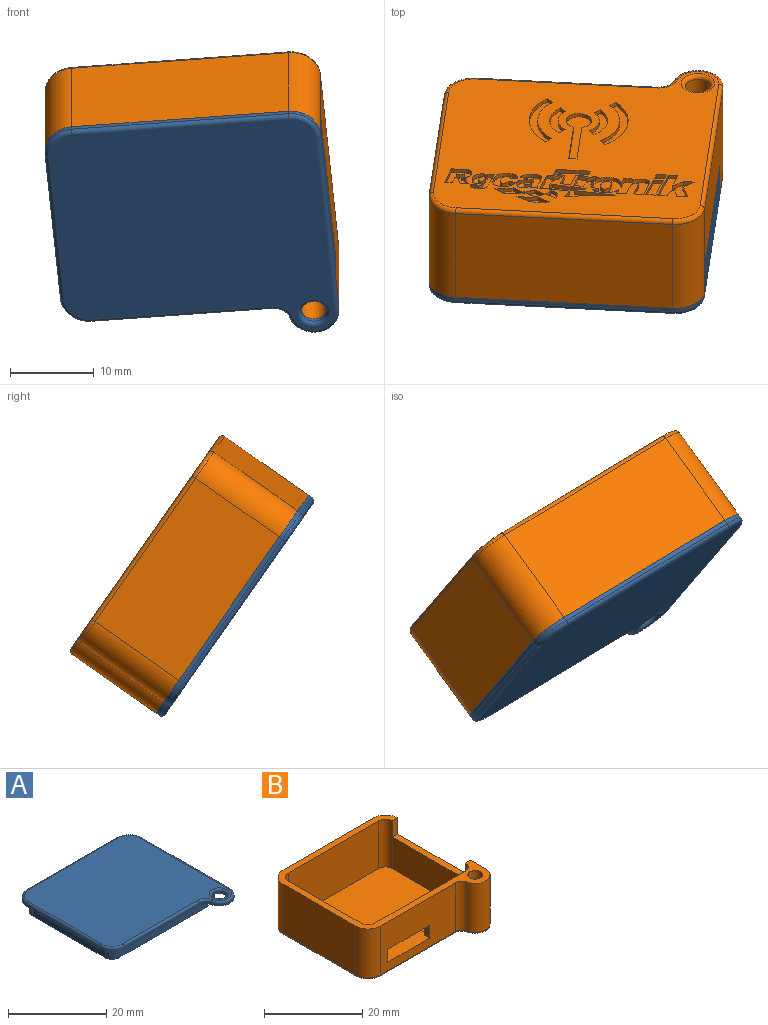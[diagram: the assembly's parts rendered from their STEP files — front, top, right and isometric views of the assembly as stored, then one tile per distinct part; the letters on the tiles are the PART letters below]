
ASSEMBLY  parts=2 mates=1
PART A: 39 faces, bbox 33.6x32.5x5 mm
  f0: plane 33x31.91mm, normal (0,0,-1), area 820.6mm2, adj f1,f2,f3,f4,f5,f6,f7,f8
  f1: plane 25.48x3mm, normal (0,1,0), area 76.4mm2, adj f0,f2,f9,f13
  f2: cylinder r=2mm len=3mm, axis (0,0,1), area 9.4mm2, adj f0,f1,f3,f13
  f3: plane 20.96x3mm, normal (-1,0,0), area 62.9mm2, adj f0,f2,f4,f13
  f4: cylinder r=2mm len=3mm, axis (0,0,1), area 9.4mm2, adj f0,f3,f5,f13
  f5: plane 25.48x3mm, normal (0,-1,0), area 76.4mm2, adj f0,f4,f6,f13
  f6: cylinder r=0.5mm len=3mm, axis (0,0,1), area 4.7mm2, adj f0,f5,f7,f13
  f7: plane 25.48x3mm, normal (0,1,0), area 76.4mm2, adj f0,f6,f10,f13
  f8: plane 25.48x3mm, normal (0,-1,0), area 76.4mm2, adj f0,f9,f12,f13
  f9: cylinder r=0.5mm len=3mm, axis (0,0,1), area 4.7mm2, adj f0,f1,f8,f13
  f10: cylinder r=1mm len=3mm, axis (0,0,1), area 4.7mm2, adj f0,f7,f11,f13
  f11: plane 20.96x3mm, normal (1,0,0), area 62.9mm2, adj f0,f10,f12,f13
  f12: cylinder r=1mm len=3mm, axis (0,0,1), area 4.7mm2, adj f0,f8,f11,f13
  f13: plane 27.98x24.96mm, normal (0,0,-1), area 77.4mm2, adj f1,f2,f3,f4,f5,f6,f7,f8
  f14: plane 26x0.5mm, normal (0,1,0), area 13mm2, adj f0,f15,f23,f37
  f15: cylinder r=3.5mm len=3.5mm, axis (0,0,1), area 2.7mm2, adj f0,f14,f16,f35
  f16: plane 21x0.5mm, normal (-1,0,0), area 10.5mm2, adj f0,f15,f17,f33
  f17: cylinder r=3.5mm len=3.5mm, axis (0,0,1), area 2.7mm2, adj f0,f16,f18,f31
  f18: plane 21.62x0.5mm, normal (0,-1,0), area 10.8mm2, adj f0,f17,f19,f30
  f19: cylinder r=2mm len=1.95mm, axis (0,0,1), area 1.4mm2, adj f0,f18,f20,f32
  f20: cylinder r=3mm len=5.93mm, axis (0,0,1), area 4.4mm2, adj f0,f19,f21,f34
  f21: plane 25.41x4.5mm, normal (1,0,0), area 96.3mm2, adj f0,f20,f23,f25,f26,f27,f36
  f22: cylinder r=1.5mm len=3mm, axis (0,0,1), area 4.7mm2, adj f0,f29
  f23: cylinder r=3.5mm len=3.5mm, axis (0,0,1), area 2.7mm2, adj f0,f14,f21,f38
  f24: plane 32x30.91mm, normal (0,0,1), area 863.6mm2, adj f29,f30,f31,f32,f33,f34,f35,f36
  f25: plane 4x1.5mm, normal (0,-1,0), area 6mm2, adj f0,f21,f26,f28
  f26: plane 20.9x1.5mm, normal (0,0,-1), area 31.3mm2, adj f21,f25,f27,f28
  f27: plane 4x1.5mm, normal (0,1,0), area 6mm2, adj f0,f21,f26,f28
  f28: plane 20.9x4mm, normal (-1,0,0), area 83.6mm2, adj f0,f25,f26,f27
  f29: torus R=2mm, axis (0,0,1), area 8.3mm2, adj f22,f24
  f30: cylinder r=0.5mm len=21.62mm, axis (1,0,0), area 17mm2, adj f18,f24,f31,f32
  f31: torus R=3mm, axis (0,0,1), area 4.1mm2, adj f17,f24,f30,f33
  f32: torus R=2.5mm, axis (0,0,1), area 2.3mm2, adj f19,f24,f30,f34
  f33: cylinder r=0.5mm len=21mm, axis (0,-1,0), area 16.5mm2, adj f16,f24,f31,f35
  f34: torus R=2.5mm, axis (0,0,1), area 6.5mm2, adj f20,f24,f32,f36
  f35: torus R=3mm, axis (0,0,1), area 4.1mm2, adj f15,f24,f33,f37
  f36: cylinder r=0.5mm len=25.41mm, axis (0,1,0), area 20mm2, adj f21,f24,f34,f38
  f37: cylinder r=0.5mm len=26mm, axis (-1,0,0), area 20.4mm2, adj f14,f24,f35,f38
  f38: torus R=3mm, axis (0,0,1), area 4.1mm2, adj f23,f24,f36,f37
PART B: 193 faces, bbox 33.6x32.5x12.7 mm
  f0: plane 30x25mm, normal (0,0,1), area 671.6mm2, adj f2,f4,f5,f6,f7,f8,f9,f10
  f1: plane 32x30.91mm, normal (0,0,-1), area 738.5mm2, adj f21,f22,f23,f24,f25,f26,f27,f28
  f2: plane 21x7.9mm, normal (-1,0,0), area 165.9mm2, adj f0,f7,f8,f31
  f3: plane 33x31.91mm, normal (0,0,1), area 151.3mm2, adj f4,f5,f6,f7,f8,f9,f10,f11
  f4: plane 26x11.9mm, normal (0,-1,0), area 309.4mm2, adj f0,f3,f7,f10
  f5: plane 21x11.9mm, normal (1,0,0), area 249.9mm2, adj f0,f3,f9,f10
  f6: plane 26x11.9mm, normal (0,1,0), area 244mm2, adj f0,f3,f8,f9,f34,f35,f36,f37
  f7: cylinder r=2mm len=11.9mm, axis (0,0,-1), area 37.4mm2, adj f0,f2,f3,f4,f33
  f8: cylinder r=2mm len=11.9mm, axis (0,0,-1), area 37.4mm2, adj f0,f2,f3,f6,f32
  f9: cylinder r=2mm len=11.9mm, axis (0,0,-1), area 37.4mm2, adj f0,f3,f5,f6,f192
  f10: cylinder r=2mm len=11.9mm, axis (0,0,-1), area 37.4mm2, adj f0,f3,f4,f5
  f11: plane 26x12.2mm, normal (0,1,0), area 317.2mm2, adj f3,f12,f19,f28
  f12: cylinder r=3.5mm len=12.2mm, axis (0,0,-1), area 67.1mm2, adj f3,f11,f13,f26
  f13: plane 21x12.2mm, normal (-1,0,0), area 256.2mm2, adj f3,f12,f14,f24
  f14: cylinder r=3.5mm len=12.2mm, axis (0,0,-1), area 67.1mm2, adj f3,f13,f15,f22
  f15: plane 21.62x12.2mm, normal (0,-1,0), area 225.4mm2, adj f3,f14,f16,f21,f34,f35,f36,f37
  f16: cylinder r=2mm len=12.2mm, axis (0,0,-1), area 33mm2, adj f3,f15,f17,f23
  f17: cylinder r=3mm len=12.2mm, axis (0,0,-1), area 107mm2, adj f3,f16,f18,f25
  f18: plane 25.41x12.2mm, normal (1,0,0), area 226.1mm2, adj f3,f17,f19,f27,f31,f32
  f19: cylinder r=3.5mm len=12.2mm, axis (0,0,-1), area 67.1mm2, adj f3,f11,f18,f29,f33
  f20: cylinder r=1.5mm len=12.2mm, axis (0,0,-1), area 115mm2, adj f3,f30
  f21: cylinder r=0.5mm len=21.62mm, axis (1,0,0), area 17mm2, adj f1,f15,f22,f23
  f22: torus R=3mm, axis (0,0,1), area 4.1mm2, adj f1,f14,f21,f24
  f23: torus R=2.5mm, axis (0,0,1), area 2.3mm2, adj f1,f16,f21,f25
  f24: cylinder r=0.5mm len=21mm, axis (0,-1,0), area 16.5mm2, adj f1,f13,f22,f26
  f25: torus R=2.5mm, axis (0,0,1), area 6.5mm2, adj f1,f17,f23,f27
  f26: torus R=3mm, axis (0,0,1), area 4.1mm2, adj f1,f12,f24,f28
  f27: cylinder r=0.5mm len=25.41mm, axis (0,1,0), area 20mm2, adj f1,f18,f25,f29
  f28: cylinder r=0.5mm len=26mm, axis (-1,0,0), area 20.4mm2, adj f1,f11,f26,f29
  f29: torus R=3mm, axis (0,0,1), area 4.1mm2, adj f1,f19,f27,f28
  f30: torus R=2mm, axis (0,0,1), area 8.3mm2, adj f1,f20
  f31: plane 21x1.5mm, normal (0,0,1), area 31.5mm2, adj f2,f18,f32,f33
  f32: plane 4x1.5mm, normal (0,1,0), area 6mm2, adj f3,f8,f18,f31
  f33: plane 4x1.5mm, normal (0,-1,0), area 6mm2, adj f3,f7,f19,f31
  f34: plane 3.2x1.5mm, normal (1,0,0), area 4.8mm2, adj f6,f15,f35,f37
  f35: plane 15x6.5mm, normal (0,0,1), area 93mm2, adj f6,f15,f34,f36,f190,f191,f192
  f36: plane 3.2x1.5mm, normal (-1,0,0), area 4.8mm2, adj f6,f15,f35,f37
  f37: plane 12x1.5mm, normal (0,0,-1), area 18mm2, adj f6,f15,f34,f36
  f38: plane 2.92x0.56mm, normal (0.98,0.19,0), area 1.5mm2, adj f1,f39,f48,f49
  f39: plane 0.93x0.5mm, normal (0.02,-1,0), area 0.5mm2, adj f1,f38,f40,f49
  f40: extruded ~1.23x0.96mm, area 1.4mm2, adj f1,f39,f41,f49
  f41: plane 0.95x0.5mm, normal (0,-1,0), area 0.5mm2, adj f1,f40,f42,f49
  f42: extruded ~1.25x0.65mm, area 0.7mm2, adj f1,f41,f43,f49
  f43: extruded ~1.67x1.11mm, area 1.7mm2, adj f1,f42,f48,f49
  f44: extruded ~0.58x0.53mm, area 0.6mm2, adj f45,f47,f49,f50
  f45: plane 0.5x0.44mm, normal (0,1,0), area 0.2mm2, adj f44,f46,f49,f50
  f46: plane 0.58x0.5mm, normal (-0.98,-0.19,0), area 0.3mm2, adj f45,f47,f49,f50
  f47: plane 0.5x0.5mm, normal (0,-1,0), area 0.2mm2, adj f44,f46,f49,f50
  f48: plane 1.83x0.5mm, normal (0,1,0), area 0.9mm2, adj f1,f38,f43,f49
  f49: plane 3.22x2.95mm, normal (0,0,-1), area 6.1mm2, adj f38,f39,f40,f41,f42,f43,f44,f45
  f50: plane 0.97x0.58mm, normal (0,0,-1), area 0.5mm2, adj f44,f45,f46,f47
  f51: cylinder r=2.45mm len=3.72mm, axis (0,0,-1), area 2.1mm2, adj f1,f52,f54,f55
  f52: plane 0.8x0.6mm, normal (0.8,-0.6,0), area 0.5mm2, adj f1,f51,f53,f55
  f53: cylinder r=3.45mm len=5.24mm, axis (0,0,-1), area 3mm2, adj f1,f52,f54,f55
  f54: plane 0.71x0.7mm, normal (0.71,0.7,0), area 0.5mm2, adj f1,f51,f53,f55
  f55: plane 5.24x1.99mm, normal (0,0,-1), area 5.1mm2, adj f51,f52,f53,f54
  f56: plane 6.59x0.5mm, normal (-1,0,0), area 3.3mm2, adj f1,f57,f59,f60
  f57: cylinder r=1.5mm len=3mm, axis (0,0,-1), area 4.2mm2, adj f1,f56,f58,f60
  f58: plane 6.59x0.5mm, normal (1,0,0), area 3.3mm2, adj f1,f57,f59,f60
  f59: plane 1x0.5mm, normal (0,-1,0), area 0.5mm2, adj f1,f56,f58,f60
  f60: plane 9.5x3mm, normal (0,0,-1), area 13.6mm2, adj f56,f57,f58,f59
  f61: plane 0.71x0.7mm, normal (0.71,0.7,0), area 0.5mm2, adj f1,f62,f64,f65
  f62: cylinder r=4.91mm len=7.44mm, axis (0,0,-1), area 4.2mm2, adj f1,f61,f63,f65
  f63: plane 0.8x0.6mm, normal (0.8,-0.6,0), area 0.5mm2, adj f1,f62,f64,f65
  f64: cylinder r=5.91mm len=8.96mm, axis (0,0,-1), area 5.1mm2, adj f1,f61,f63,f65
  f65: plane 8.96x2.97mm, normal (0,0,-1), area 9.3mm2, adj f61,f62,f63,f64
  f66: extruded ~2.89x2.89mm, area 4.2mm2, adj f1,f67,f69,f70
  f67: plane 0.84x0.5mm, normal (-0.14,0.99,0), area 0.4mm2, adj f1,f66,f68,f70
  f68: extruded ~1.46x1.18mm, area 1.8mm2, adj f1,f67,f69,f70
  f69: plane 0.84x0.5mm, normal (-0.06,-1,0), area 0.4mm2, adj f1,f66,f68,f70
  f70: plane 2.9x2.9mm, normal (0,0,-1), area 4.8mm2, adj f66,f67,f68,f69
  f71: plane 1.44x0.5mm, normal (0,-1,0), area 0.7mm2, adj f1,f72,f78,f79
  f72: plane 1.07x0.5mm, normal (-0.98,-0.19,0), area 0.5mm2, adj f1,f71,f73,f79
  f73: plane 4.07x0.5mm, normal (0,1,0), area 2mm2, adj f1,f72,f74,f79
  f74: plane 1.08x0.5mm, normal (0.98,0.19,0), area 0.6mm2, adj f1,f73,f75,f79
  f75: plane 1.32x0.5mm, normal (0,-1,0), area 0.7mm2, adj f1,f74,f76,f79
  f76: plane 1.81x0.5mm, normal (0.98,0.21,0), area 0.9mm2, adj f1,f75,f77,f79
  f77: plane 1.24x0.5mm, normal (0.12,-0.99,0), area 0.6mm2, adj f1,f76,f78,f79
  f78: plane 1.99x0.5mm, normal (-0.97,-0.22,0), area 1mm2, adj f1,f71,f77,f79
  f79: plane 4.27x3.05mm, normal (0,0,-1), area 6.8mm2, adj f71,f72,f73,f74,f75,f76,f77,f78
  f80: plane 3.11x0.65mm, normal (-0.98,-0.21,0), area 1.6mm2, adj f1,f81,f83,f84
  f81: plane 1.19x0.5mm, normal (0,1,0), area 0.6mm2, adj f1,f80,f82,f84
  f82: plane 3.11x0.65mm, normal (0.98,0.21,0), area 1.6mm2, adj f1,f81,f83,f84
  f83: plane 1.19x0.5mm, normal (0,-1,0), area 0.6mm2, adj f1,f80,f82,f84
  f84: plane 3.11x1.84mm, normal (0,0,-1), area 3.7mm2, adj f80,f81,f82,f83
  f85: extruded ~2.19x0.5mm, area 1.1mm2, adj f1,f86,f88,f89
  f86: plane 1.18x0.8mm, normal (0.56,-0.83,0), area 0.7mm2, adj f1,f85,f87,f89
  f87: extruded ~2.46x0.5mm, area 1.2mm2, adj f1,f86,f88,f89
  f88: plane 1.45x0.95mm, normal (-0.55,0.84,0), area 0.9mm2, adj f1,f85,f87,f89
  f89: plane 3.64x1.16mm, normal (0,0,-1), area 2.4mm2, adj f85,f86,f87,f88
  f90: extruded ~2.45x0.5mm, area 1.2mm2, adj f1,f91,f93,f94
  f91: plane 1.73x0.92mm, normal (0.47,-0.88,0), area 1mm2, adj f1,f90,f92,f94
  f92: extruded ~2.2x0.5mm, area 1.1mm2, adj f1,f91,f93,f94
  f93: plane 1.49x0.97mm, normal (-0.55,0.84,0), area 0.9mm2, adj f1,f90,f92,f94
  f94: plane 3.93x1.14mm, normal (0,0,-1), area 2.5mm2, adj f90,f91,f92,f93
  f95: plane 1.27x0.84mm, normal (-0.55,0.83,0), area 0.8mm2, adj f1,f96,f98,f99
  f96: extruded ~1.29x0.56mm, area 0.7mm2, adj f1,f95,f97,f99
  f97: plane 1.28x0.83mm, normal (0.55,-0.84,0), area 0.8mm2, adj f1,f96,f98,f99
  f98: extruded ~1.28x0.55mm, area 0.7mm2, adj f1,f95,f97,f99
  f99: plane 2.55x1.39mm, normal (0,0,-1), area 1.8mm2, adj f95,f96,f97,f98
  f100: plane 0.83x0.64mm, normal (-0.61,0.79,0), area 0.5mm2, adj f1,f101,f103,f104
  f101: extruded ~0.87x0.62mm, area 0.5mm2, adj f1,f100,f102,f104
  f102: plane 1.28x0.85mm, normal (0.55,-0.83,0), area 0.8mm2, adj f1,f101,f103,f104
  f103: extruded ~1.08x0.5mm, area 0.6mm2, adj f1,f100,f102,f104
  f104: plane 1.72x1.47mm, normal (0,0,-1), area 1.3mm2, adj f100,f101,f102,f103
  f105: plane 0.8x0.6mm, normal (-0.8,-0.6,0), area 0.5mm2, adj f1,f106,f108,f109
  f106: cylinder r=4.91mm len=7.44mm, axis (0,0,-1), area 4.2mm2, adj f1,f105,f107,f109
  f107: plane 0.71x0.7mm, normal (-0.71,0.7,0), area 0.5mm2, adj f1,f106,f108,f109
  f108: cylinder r=5.91mm len=8.96mm, axis (0,0,-1), area 5.1mm2, adj f1,f105,f107,f109
  f109: plane 8.96x2.97mm, normal (0,0,-1), area 9.3mm2, adj f105,f106,f107,f108
  f110: plane 0.8x0.6mm, normal (-0.8,-0.6,0), area 0.5mm2, adj f1,f111,f113,f114
  f111: cylinder r=2.45mm len=3.72mm, axis (0,0,-1), area 2.1mm2, adj f1,f110,f112,f114
  f112: plane 0.71x0.7mm, normal (-0.71,0.7,0), area 0.5mm2, adj f1,f111,f113,f114
  f113: cylinder r=3.45mm len=5.24mm, axis (0,0,-1), area 3mm2, adj f1,f110,f112,f114
  f114: plane 5.24x1.99mm, normal (0,0,-1), area 5.1mm2, adj f110,f111,f112,f113
  f115: plane 1.98x0.5mm, normal (-0.98,-0.21,0), area 1mm2, adj f1,f116,f136,f138
  f116: extruded ~2.08x1.17mm, area 1.6mm2, adj f1,f115,f117,f138
  f117: plane 0.5x0.49mm, normal (-0.98,-0.18,0), area 0.2mm2, adj f1,f116,f118,f138
  f118: plane 1.13x0.5mm, normal (0,1,0), area 0.6mm2, adj f1,f117,f119,f138
  f119: plane 1.13x0.5mm, normal (0.98,0.18,0), area 0.6mm2, adj f1,f118,f120,f138
  f120: extruded ~3.1x1.2mm, area 1.9mm2, adj f1,f119,f121,f138
  f121: plane 0.5x0.48mm, normal (-0.9,-0.45,0), area 0.3mm2, adj f1,f120,f122,f138
  f122: extruded ~1.37x0.71mm, area 0.8mm2, adj f1,f121,f123,f138
  f123: plane 0.61x0.5mm, normal (-0.98,-0.19,0), area 0.3mm2, adj f1,f122,f124,f138
  f124: plane 1.13x0.5mm, normal (0,1,0), area 0.6mm2, adj f1,f123,f125,f138
  f125: plane 1.89x0.5mm, normal (0.98,0.21,0), area 1mm2, adj f1,f124,f126,f138
  f126: plane 1.16x0.5mm, normal (0.13,-0.99,0), area 0.6mm2, adj f1,f125,f127,f138
  f127: extruded ~1.29x1.11mm, area 1.6mm2, adj f1,f126,f128,f138
  f128: plane 0.86x0.5mm, normal (0.15,-0.99,0), area 0.4mm2, adj f1,f127,f129,f138
  f129: plane 0.71x0.5mm, normal (0.3,0.96,0), area 0.4mm2, adj f1,f128,f130,f138
  f130: extruded ~3.11x0.78mm, area 1.8mm2, adj f1,f129,f131,f138
  f131: plane 0.75x0.5mm, normal (0.97,0.23,0), area 0.4mm2, adj f1,f130,f132,f138
  f132: plane 1.2x0.5mm, normal (0,-1,0), area 0.6mm2, adj f1,f131,f133,f138
  f133: plane 1.52x0.5mm, normal (-0.98,-0.21,0), area 0.8mm2, adj f1,f132,f134,f138
  f134: extruded ~0.96x0.82mm, area 1mm2, adj f1,f133,f135,f138
  f135: plane 1.44x0.5mm, normal (0.98,0.2,0), area 0.7mm2, adj f1,f134,f136,f138
  f136: plane 1.2x0.5mm, normal (0,-1,0), area 0.6mm2, adj f1,f115,f135,f138
  f137: extruded ~1.64x1.26mm, area 2.3mm2, adj f138,f188
  f138: plane 8.98x3.23mm, normal (0,0,-1), area 18.9mm2, adj f115,f116,f117,f118,f119,f120,f121,f122
  f139: plane 0.77x0.5mm, normal (-0.13,0.99,0), area 0.4mm2, adj f1,f140,f145,f146
  f140: extruded ~2.29x1.26mm, area 1.8mm2, adj f1,f139,f141,f146
  f141: plane 1.75x0.5mm, normal (-0.98,-0.21,0), area 0.9mm2, adj f1,f140,f142,f146
  f142: plane 0.75x0.5mm, normal (0,1,0), area 0.4mm2, adj f1,f141,f143,f146
  f143: plane 0.5x0.3mm, normal (0.97,0.25,0), area 0.2mm2, adj f1,f142,f145,f146
  f144: extruded ~1x0.74mm, area 1.4mm2, adj f146,f189
  f145: extruded ~2.57x1.72mm, area 2.7mm2, adj f1,f139,f143,f146
  f146: plane 3.08x2.67mm, normal (0,0,-1), area 5.2mm2, adj f139,f140,f141,f142,f143,f144,f145
  f147: extruded ~2.8x2.52mm, area 2.8mm2, adj f1,f148,f152,f153
  f148: plane 0.87x0.5mm, normal (0.09,-1,0), area 0.4mm2, adj f1,f147,f149,f153
  f149: extruded ~2.25x1.95mm, area 3mm2, adj f1,f148,f152,f153
  f150: plane 0.5x0.1mm, normal (0.98,0.22,0), area 0mm2, adj f151,f153,f154
  f151: extruded ~0.86x0.69mm, area 1.2mm2, adj f150,f153,f154
  f152: plane 0.9x0.5mm, normal (0,-1,0), area 0.4mm2, adj f1,f147,f149,f153
  f153: plane 2.9x2.85mm, normal (0,0,-1), area 5.5mm2, adj f147,f148,f149,f150,f151,f152
  f154: plane 0.87x0.7mm, normal (0,0,-1), area 0.4mm2, adj f150,f151
  f155: plane 0.81x0.5mm, normal (-0.91,-0.41,0), area 0.4mm2, adj f1,f156,f168,f169
  f156: extruded ~1.09x0.61mm, area 0.7mm2, adj f1,f155,f157,f169
  f157: plane 0.53x0.5mm, normal (-0.97,-0.22,0), area 0.3mm2, adj f1,f156,f158,f169
  f158: plane 0.85x0.5mm, normal (0,1,0), area 0.4mm2, adj f1,f157,f159,f169
  f159: plane 2.72x0.66mm, normal (0.97,0.23,0), area 1.4mm2, adj f1,f158,f160,f169
  f160: plane 0.5x0.5mm, normal (0,-1,0), area 0.2mm2, adj f1,f159,f161,f169
  f161: plane 3.1x0.5mm, normal (0.1,-0.99,0), area 1.6mm2, adj f1,f160,f162,f169
  f162: plane 1.12x0.5mm, normal (0.93,0.37,0), area 0.6mm2, adj f1,f161,f163,f169
  f163: plane 6x0.77mm, normal (-0.13,-0.99,0), area 3mm2, adj f1,f162,f164,f169
  f164: plane 5.02x0.51mm, normal (-0.1,0.99,0), area 2.5mm2, adj f1,f163,f165,f169
  f165: plane 1.41x0.53mm, normal (-0.35,-0.94,0), area 0.8mm2, adj f1,f164,f166,f169
  f166: plane 4.04x0.55mm, normal (-0.13,0.99,0), area 2mm2, adj f1,f165,f167,f169
  f167: plane 0.5x0.39mm, normal (0.54,0.84,0), area 0.2mm2, adj f1,f166,f168,f169
  f168: extruded ~1.26x1mm, area 0.9mm2, adj f1,f155,f167,f169
  f169: plane 9.15x4.23mm, normal (0,0,-1), area 10.4mm2, adj f155,f156,f157,f158,f159,f160,f161,f162
  f170: plane 0.81x0.5mm, normal (0.98,0.19,0), area 0.4mm2, adj f1,f171,f173,f174
  f171: plane 1.2x0.5mm, normal (0,-1,0), area 0.6mm2, adj f1,f170,f172,f174
  f172: plane 0.81x0.5mm, normal (-0.98,-0.2,0), area 0.4mm2, adj f1,f171,f173,f174
  f173: plane 1.21x0.5mm, normal (0,1,0), area 0.6mm2, adj f1,f170,f172,f174
  f174: plane 1.36x0.81mm, normal (0,0,-1), area 1mm2, adj f170,f171,f172,f173
  f175: plane 2.25x0.5mm, normal (-0.98,-0.2,0), area 1.1mm2, adj f1,f176,f186,f187
  f176: plane 1.15x0.5mm, normal (0,1,0), area 0.6mm2, adj f1,f175,f177,f187
  f177: plane 4.3x0.93mm, normal (0.98,0.21,0), area 2.2mm2, adj f1,f176,f178,f187
  f178: plane 1.16x0.5mm, normal (0,-1,0), area 0.6mm2, adj f1,f177,f179,f187
  f179: plane 0.76x0.5mm, normal (-0.98,-0.2,0), area 0.4mm2, adj f1,f178,f180,f187
  f180: plane 0.64x0.51mm, normal (-0.62,-0.78,0), area 0.4mm2, adj f1,f179,f181,f187
  f181: plane 1.27x0.5mm, normal (0.96,-0.28,0), area 0.7mm2, adj f1,f180,f182,f187
  f182: plane 1.33x0.5mm, normal (0,-1,0), area 0.7mm2, adj f1,f181,f183,f187
  f183: plane 2.02x0.77mm, normal (-0.93,0.36,0), area 1.1mm2, adj f1,f182,f184,f187
  f184: plane 1.3x1.08mm, normal (-0.64,-0.77,0), area 0.8mm2, adj f1,f183,f185,f187
  f185: plane 1.35x0.5mm, normal (0,1,0), area 0.7mm2, adj f1,f184,f186,f187
  f186: plane 1.23x1.05mm, normal (0.65,0.76,0), area 0.8mm2, adj f1,f175,f185,f187
  f187: plane 4.3x4.19mm, normal (0,0,-1), area 9.3mm2, adj f175,f176,f177,f178,f179,f180,f181,f182
  f188: plane 1.65x1.27mm, normal (0,0,-1), area 1.6mm2, adj f137
  f189: plane 1.01x0.74mm, normal (0,0,-1), area 0.6mm2, adj f144
  f190: plane 5x1.8mm, normal (1,0,0), area 9mm2, adj f0,f6,f35,f191
  f191: plane 15x1.8mm, normal (0,1,0), area 27mm2, adj f0,f35,f190,f192
  f192: plane 5x1.8mm, normal (-1,0,0), area 9mm2, adj f0,f9,f35,f191
PLACE A rot(axis=(1,-0.04,0.02),125.1deg) t=(46.38,13.14,33.98)mm
PLACE B rot(axis=(1,-0.04,0.02),125.1deg) t=(29.03,17.11,52.18)mm fixed
MATE slider B.f17 <-> A.f20  axis (0,-0.82,-0.57) through (59.81,20.95,24.56)mm
